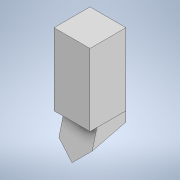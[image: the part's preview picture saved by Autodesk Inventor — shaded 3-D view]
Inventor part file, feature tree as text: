
AUTODESK INVENTOR PART (.ipt)
format: ipt  version: 2020 (Build 240168000, 168)  size: 171,520 bytes
history: native  units: mm
features: sketch x10, extrude x5, plane x5, other x5
ambient origin geometry x8: Origin, YZ Plane, XZ Plane, XY Plane, X Axis, Y Axis, Z Axis, Center Point
bodies: 实体1 (feature_tree), 实体2 (feature_tree), 实体3 (feature_tree)
feature tree (25):
  extrude  "拉伸1"  Depth=30.0mm
  sketch  "草图2"  dims[d2=10.0mm d3=10.0mm d4=0.0mm]
  plane  "工作平面4"
  other  "分割1"
  other  "三维草图1"
  other  "副正交平面"
  sketch  "草图4"  dims[d5=45.0deg d6=150.0deg]
  extrude  "拉伸2"  Depth=10.0mm TaperAngle=0.0deg
  other  "正交平面2"
  sketch  "草图6"  dims[d10=90.0deg d11=75.0deg]
  sketch  "草图7"  dims[d12=-20.0mm]
  plane  "工作平面3"
  extrude  "拉伸3"  TaperAngle=150.0deg  [1 undecoded]
  plane  "工作平面5"
  plane  "工作平面6"
  extrude  "拉伸4"  Depth=30.0mm TaperAngle=0.0deg
  sketch  "草图10"  dims[d15=20.0mm]
  plane  "工作平面8"
  extrude  "拉伸5"  TaperAngle=75.0deg  [1 undecoded]
  sketch  "草图1"  dims[d0=5.0mm d1=30.0mm]
  sketch  "草图5"  dims[d7=30.543262mm d8=30.0mm d9=0.0mm]
  other  "正交平面"
  sketch  "草图8"  dims[d13=15.0mm]
  sketch  "草图9"  dims[d14=15.0mm]
  sketch  "草图11"  dims[d16=30.0mm d17=0.0mm d18=1.745329mm d19=10.0mm d20=0.0mm d21=14.835299mm d22=10.0mm d23=0.0mm]
note: 2 required parameter values undecoded (feature->parameter linkage not recoverable at this tier; creation-order binding heuristic only, values carry confidence <= 0.55)
